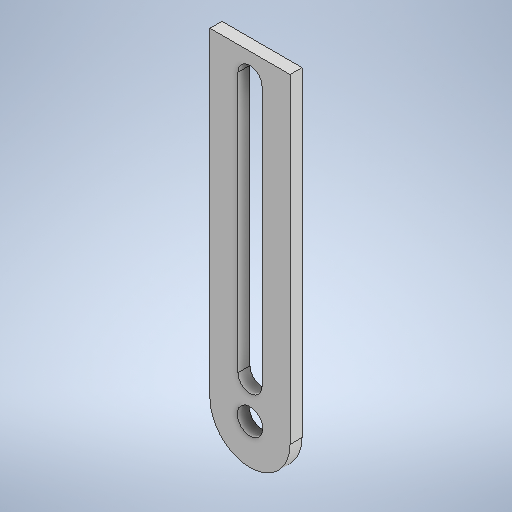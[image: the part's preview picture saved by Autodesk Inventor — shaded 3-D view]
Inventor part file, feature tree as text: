
AUTODESK INVENTOR PART (.ipt)
format: ipt  version: 2025.1 (Build 291241000, 241)  size: 264,192 bytes
history: native  units: mm
features: extrude x2, sketch x2, other x1
ambient origin geometry x8: Origin, YZ Plane, XZ Plane, XY Plane, X Axis, Y Axis, Z Axis, Center Point
bodies: Body1 (feature_tree)
feature tree (5):
  other  "ソリッド1"
  extrude  "押し出し1"  Depth=3.2mm
  extrude  "押し出し2"  Depth=10.0mm
  sketch  "スケッチ1"
  sketch  "スケッチ2"
